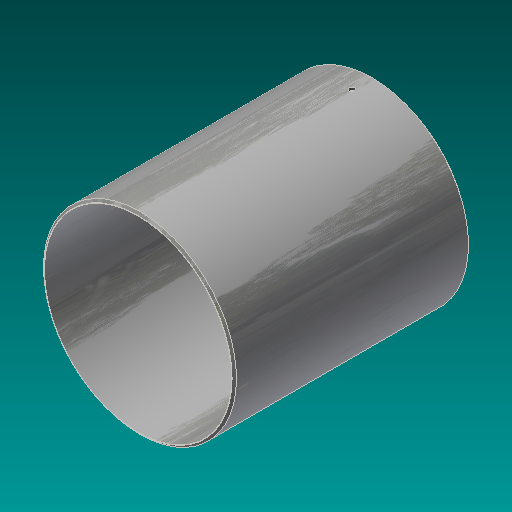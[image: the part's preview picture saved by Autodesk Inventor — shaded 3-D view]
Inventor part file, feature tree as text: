
AUTODESK INVENTOR PART (.ipt)
format: ipt  version: 2017.3 (Build 213257000, 257)  size: 212,480 bytes
history: native  units: in
note: dims shown in document units (in); Inventor stores cm internally (conversion verified against a paired STEP export)
features: chamfer x2, sketch x2, extrude x1, plane x1, hole x1, pattern_circular x1
ambient origin geometry x8: Origin, YZ Plane, XZ Plane, XY Plane, X Axis, Y Axis, Z Axis, Center Point
bodies: Solid1 (feature_tree)
feature tree (8):
  extrude  "Extrusion1"  Depth=33.0in
  chamfer  "Chamfer1"  Distance=41.5536in
  chamfer  "Chamfer2"  Distance=0.125in
  plane  "Work Plane1"
  hole  "Hole1"  [1 undecoded]
  pattern_circular  "Circular Pattern1"  [2 undecoded]
  sketch  "Sketch1"  dims[d0=34.0in d1=33.0in d2=41.5536in d3=0.0in]
  sketch  "Sketch2"  dims[d4=0.4375in d5=0.125in d6=0.2577in d7=0.4375in d8=0.125in d9=0.2577in d10=3.9062in d11=0.891in d12=0.553in d13=0.0246in d14=0.897in d15=0.375in d16=0.25in d17=0.5635in d18=0.91in d19=0.8108in d20=0.7874in d21=360.0deg]
note: 3 required parameter values undecoded (feature->parameter linkage not recoverable at this tier; creation-order binding heuristic only, values carry confidence <= 0.55)
